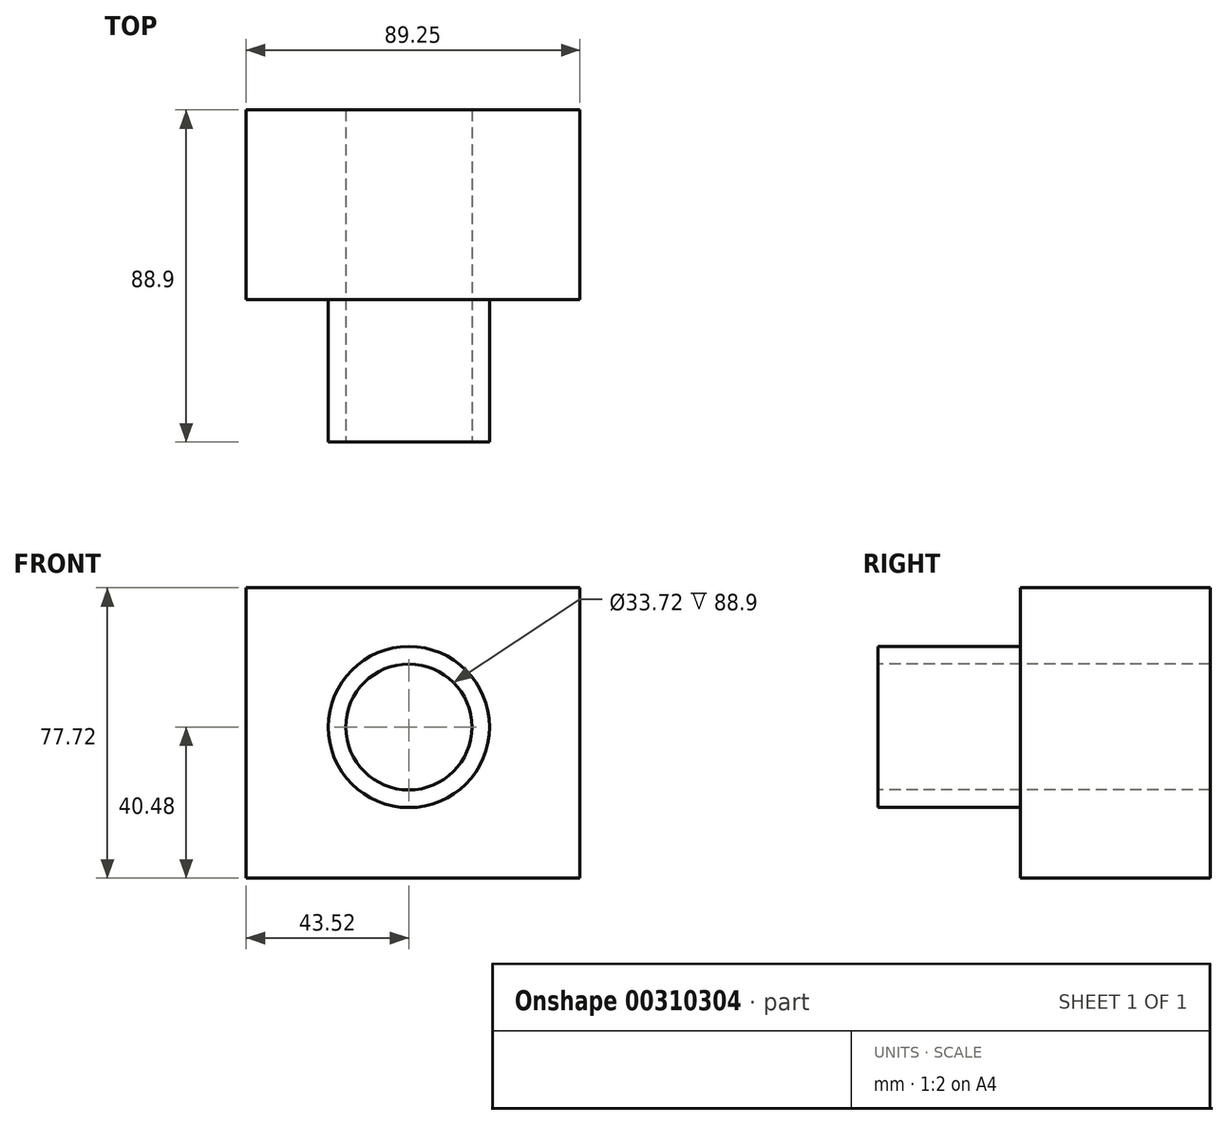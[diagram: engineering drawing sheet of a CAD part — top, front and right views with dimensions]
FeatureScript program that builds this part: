
annotation { "Feature Type Name" : "Feature", "Feature Type Description" : "" }
export const myFeature = defineFeature(function(context is Context, id is Id, definition is map)
    precondition{}
    {
        {
            var Q0;
            Q0=qCreatedBy(makeId("Front.planeOp"),FACE);
            var sketch = newSketch(context, id + "F0", { "sketchPlane" : qUnion([Q0])});
            skLineSegment(sketch, "E0.bottom", {"start": v(-43.52, 37.24) * mm, "end": v(45.73, 37.24) * mm});
            skLineSegment(sketch, "E0.top", {"start": v(-43.52, -40.48) * mm, "end": v(45.73, -40.48) * mm});
            skLineSegment(sketch, "E0.left", {"start": v(-43.52, 37.24) * mm, "end": v(-43.52, -40.48) * mm});
            skLineSegment(sketch, "E0.right", {"start": v(45.73, 37.24) * mm, "end": v(45.73, -40.48) * mm});
            skSolve(sketch);
        }
        {
            var Q0;
            Q0=makeQuery(id+"F0.imprint","IMPRINT",FACE,{"disambiguationData":[TD([[makeQuery(id+"F0.imprint","IMPRINT",EDGE,{"derivedFrom":sQuery(id+"F0.wireOp",EDGE,"E0.bottom")}),-1.0]])]});
            extrude(context, id + "F1", {"entities" : qUnion([Q0]), "depth" : 50.8 * mm});
        }
        {
            var Q0;
            Q0=makeQuery(id+"F1.opExtrude","CAP_FACE",FACE,{"disambiguationData":[OSD([sQuery(id+"F0.wireOp",EDGE,"E0.bottom"),sQuery(id+"F0.wireOp",EDGE,"E0.top"),sQuery(id+"F0.wireOp",EDGE,"E0.left"),sQuery(id+"F0.wireOp",EDGE,"E0.right")])],"isStart":false});
            var sketch = newSketch(context, id + "F2", { "sketchPlane" : qUnion([Q0])});
            skCircle(sketch, "E1", {"center": v(0, 0) * mm, "radius": 21.56 * mm});
            skSolve(sketch);
        }
        {
            var Q0;
            Q0=makeQuery(id+"F2.imprint","IMPRINT",FACE,{"disambiguationData":[TD([[makeQuery(id+"F2.imprint","IMPRINT",EDGE,{"derivedFrom":sQuery(id+"F2.wireOp",EDGE,"E1")}),1.0]])]});
            extrude(context, id + "F3", {"entities" : qUnion([Q0]), "operationType" : NewBodyOperationType.ADD, "depth" : 38.1 * mm});
        }
        {
            var Q0;
            Q0=makeQuery(id+"F3.opExtrude","CAP_FACE",FACE,{"disambiguationData":[OSD([sQuery(id+"F2.wireOp",EDGE,"E1")])],"isStart":false});
            var sketch = newSketch(context, id + "F4", { "sketchPlane" : qUnion([Q0])});
            skCircle(sketch, "E2", {"center": v(0, 0) * mm, "radius": 16.86 * mm});
            skSolve(sketch);
        }
        {
            var Q0;
            Q0=makeQuery(id+"F4.imprint","IMPRINT",FACE,{"disambiguationData":[TD([[makeQuery(id+"F4.imprint","IMPRINT",EDGE,{"derivedFrom":sQuery(id+"F4.wireOp",EDGE,"E2")}),1.0]])]});
            extrude(context, id + "F5", {"entities" : qUnion([Q0]), "operationType" : NewBodyOperationType.REMOVE, "oppositeDirection" : true, "depth" : 127 * mm});
        }
    });
